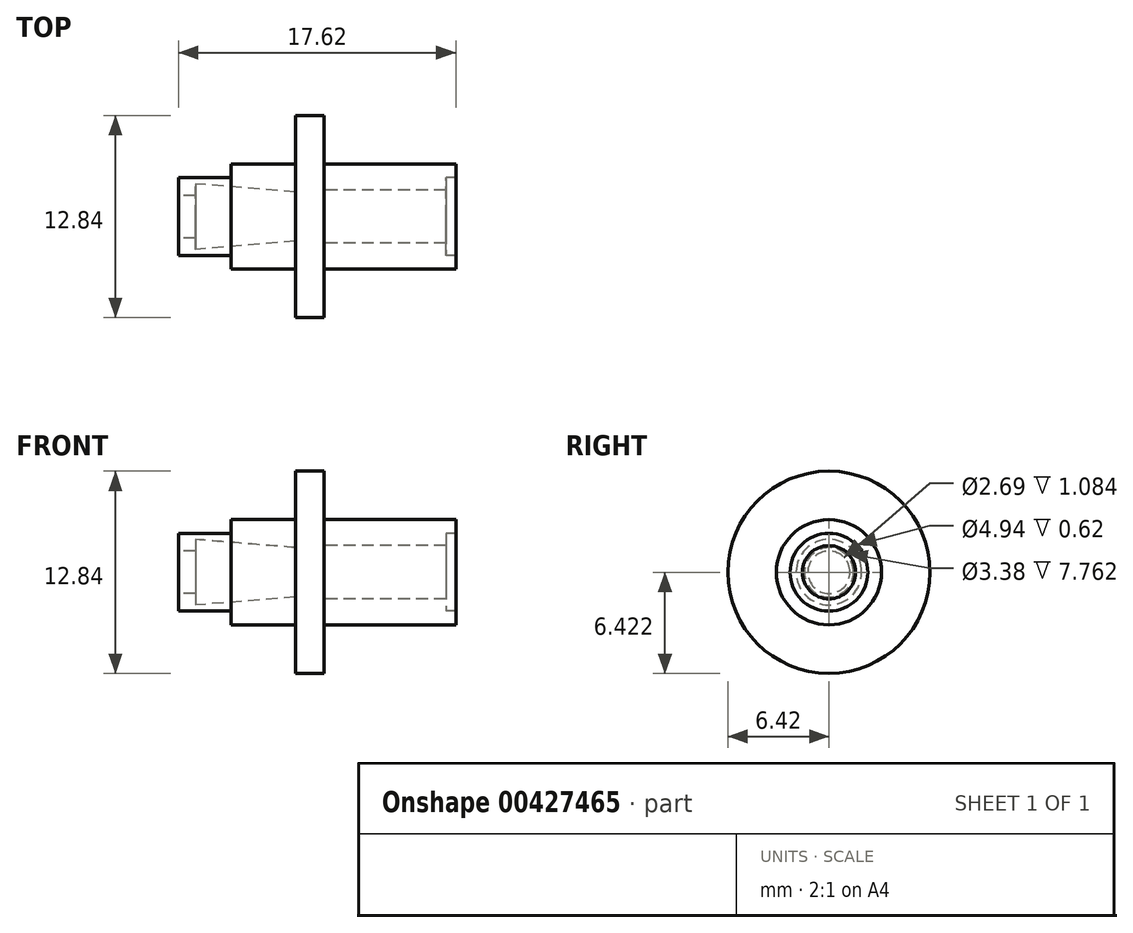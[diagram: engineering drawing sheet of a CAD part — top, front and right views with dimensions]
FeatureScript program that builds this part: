
annotation { "Feature Type Name" : "Feature", "Feature Type Description" : "" }
export const myFeature = defineFeature(function(context is Context, id is Id, definition is map)
    precondition{}
    {
        {
            var Q0;
            Q0=qCreatedBy(makeId("Front.planeOp"),FACE);
            var sketch = newSketch(context, id + "F0", { "sketchPlane" : qUnion([Q0])});
            skLineSegment(sketch, "E0", {"start": v(0, 0.91) * mm, "end": v(0, 2.47) * mm});
            skLineSegment(sketch, "E1", {"start": v(0, 2.47) * mm, "end": v(1.78, 2.47) * mm});
            skLineSegment(sketch, "E2", {"start": v(1.78, 2.47) * mm, "end": v(1.78, 0.78) * mm});
            skLineSegment(sketch, "E3", {"start": v(1.78, 0.78) * mm, "end": v(9.54, 0.78) * mm});
            skLineSegment(sketch, "E4", {"start": v(9.54, 0.87) * mm, "end": v(9.54, 0) * mm});
            skLineSegment(sketch, "E5", {"start": v(10.16, 0) * mm, "end": v(9.54, 0) * mm});
            skLineSegment(sketch, "E6", {"start": v(10.16, 0) * mm, "end": v(10.16, -0.87) * mm});
            skLineSegment(sketch, "E7", {"start": v(10.16, -0.87) * mm, "end": v(1.78, -0.87) * mm});
            skLineSegment(sketch, "E8", {"start": v(1.78, -0.87) * mm, "end": v(1.78, -3.95) * mm});
            skLineSegment(sketch, "E9", {"start": v(1.78, -3.95) * mm, "end": v(0, -3.95) * mm});
            skLineSegment(sketch, "E10", {"start": v(0, -3.95) * mm, "end": v(0, -0.87) * mm});
            skLineSegment(sketch, "E11", {"start": v(0, -0.87) * mm, "end": v(-4.12, -0.87) * mm});
            skLineSegment(sketch, "E12", {"start": v(-4.12, -0.87) * mm, "end": v(-4.12, 0) * mm});
            skLineSegment(sketch, "E13", {"start": v(-4.12, 0) * mm, "end": v(-7.46, 0) * mm});
            skLineSegment(sketch, "E14", {"start": v(-7.46, 0) * mm, "end": v(-7.46, 1.13) * mm});
            skLineSegment(sketch, "E15", {"start": v(-7.46, 1.13) * mm, "end": v(-6.37, 1.13) * mm});
            skLineSegment(sketch, "E16", {"start": v(-6.37, 1.13) * mm, "end": v(-6.37, 0.4) * mm});
            skLineSegment(sketch, "E17", {"start": v(-6.37, 0.4) * mm, "end": v(0, 0.91) * mm});
            skSolve(sketch);
        }
        {
            var Q0;
            Q0=makeQuery(id+"F0.imprint","IMPRINT",FACE,{"disambiguationData":[TD([[makeQuery(id+"F0.imprint","IMPRINT",EDGE,{"derivedFrom":sQuery(id+"F0.wireOp",EDGE,"E0")}),-1.0]])]});
            var Q1;
            Q1=sQuery(id+"F0.wireOp",EDGE,"E1");
            revolve(context, id + "F1", {"entities" : qUnion([Q0]), "axis" : qUnion([Q1]), "revolveType" : RevolveType.FULL});
        }
    });
